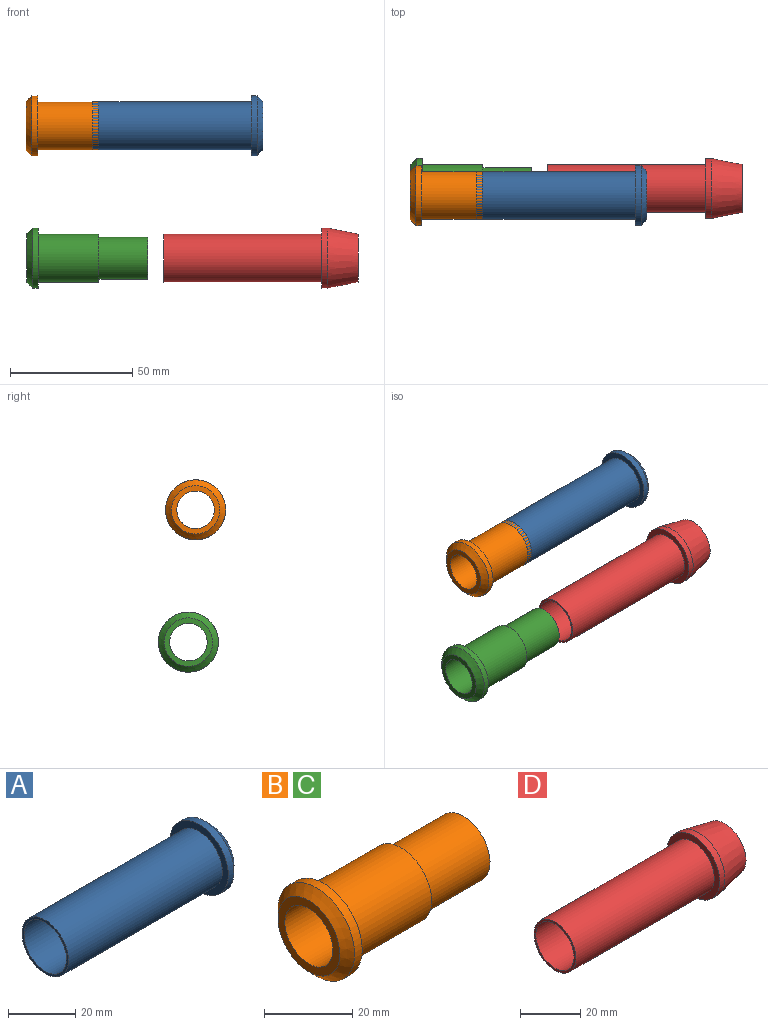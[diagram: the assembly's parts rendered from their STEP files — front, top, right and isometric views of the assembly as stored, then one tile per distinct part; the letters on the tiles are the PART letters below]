
ASSEMBLY  parts=4 mates=2
PART A: 9 faces, bbox 69.6x24.6x24.6 mm
  f0: plane 24.6x24.6mm, normal (-1,0,0), area 173.6mm2, adj f1,f8
  f1: cylinder r=9.8mm len=64.8mm, axis (-1,0,0), area 3990.1mm2, adj f0,f2
  f2: plane 19.6x19.6mm, normal (-1,0,0), area 50.1mm2, adj f1,f3
  f3: cylinder r=8.95mm len=20mm, axis (-1,0,0), area 1124.7mm2, adj f2,f4
  f4: plane 17.9x17.9mm, normal (-1,0,0), area 65.4mm2, adj f3,f5
  f5: cylinder r=7.7mm len=49.6mm, axis (-1,0,0), area 2399.7mm2, adj f4,f6
  f6: plane 19.83x19.83mm, normal (1,0,0), area 122.7mm2, adj f5,f7
  f7: cone r=9.92mm half-angle=45deg, axis (-1,0,0), area 235.2mm2, adj f6,f8
  f8: cylinder r=12.3mm len=24.6mm, axis (-1,0,0), area 186.8mm2, adj f0,f7
PART B: 9 faces, bbox 49.6x24.6x24.6 mm
  f0: cylinder r=9.8mm len=24.8mm, axis (1,0,0), area 1527.1mm2, adj f1,f8
  f1: plane 24.6x24.6mm, normal (1,0,0), area 173.6mm2, adj f0,f2
  f2: cylinder r=12.3mm len=24.6mm, axis (1,0,0), area 186.8mm2, adj f1,f3
  f3: cone r=9.92mm half-angle=45deg, axis (1,0,0), area 235.2mm2, adj f2,f4
  f4: plane 19.83x19.83mm, normal (-1,0,0), area 122.7mm2, adj f3,f5
  f5: cylinder r=7.7mm len=49.6mm, axis (1,0,0), area 2399.7mm2, adj f4,f6
  f6: plane 17.1x17.1mm, normal (1,0,0), area 43.4mm2, adj f5,f7
  f7: cylinder r=8.55mm len=20mm, axis (1,0,0), area 1074.4mm2, adj f6,f8
  f8: plane 19.6x19.6mm, normal (1,0,0), area 72.1mm2, adj f0,f7
PART C: same geometry as B
PART D: 9 faces, bbox 79.6x24.6x24.6 mm
  f0: plane 24.6x24.6mm, normal (-1,0,0), area 173.6mm2, adj f1,f8
  f1: cylinder r=9.8mm len=64.8mm, axis (-1,0,0), area 3990.1mm2, adj f0,f2
  f2: plane 19.6x19.6mm, normal (-1,0,0), area 50.1mm2, adj f1,f3
  f3: cylinder r=8.95mm len=20mm, axis (-1,0,0), area 1124.7mm2, adj f2,f4
  f4: plane 17.9x17.9mm, normal (-1,0,0), area 65.4mm2, adj f3,f5
  f5: cylinder r=7.7mm len=59.6mm, axis (-1,0,0), area 2883.5mm2, adj f4,f6
  f6: plane 19.67x19.67mm, normal (1,0,0), area 117.7mm2, adj f5,f7
  f7: cone r=9.84mm half-angle=11.3deg, axis (-1,0,0), area 873.7mm2, adj f6,f8
  f8: cylinder r=12.3mm len=24.6mm, axis (-1,0,0), area 191.7mm2, adj f0,f7
PLACE A t=(0.71,4.77,12.66)mm
PLACE B t=(3.27,4.77,12.66)mm
PLACE C t=(3.57,7.75,-41.54)mm
PLACE D t=(29.69,7.75,-41.54)mm
MATE slider C.f0 <-> D.f1  axis (1,0,0) through (3.37,7.75,-41.54)mm
MATE cylindrical A.f1 <-> B.f0  axis (-1,0,0) through (-19.09,4.77,12.66)mm
